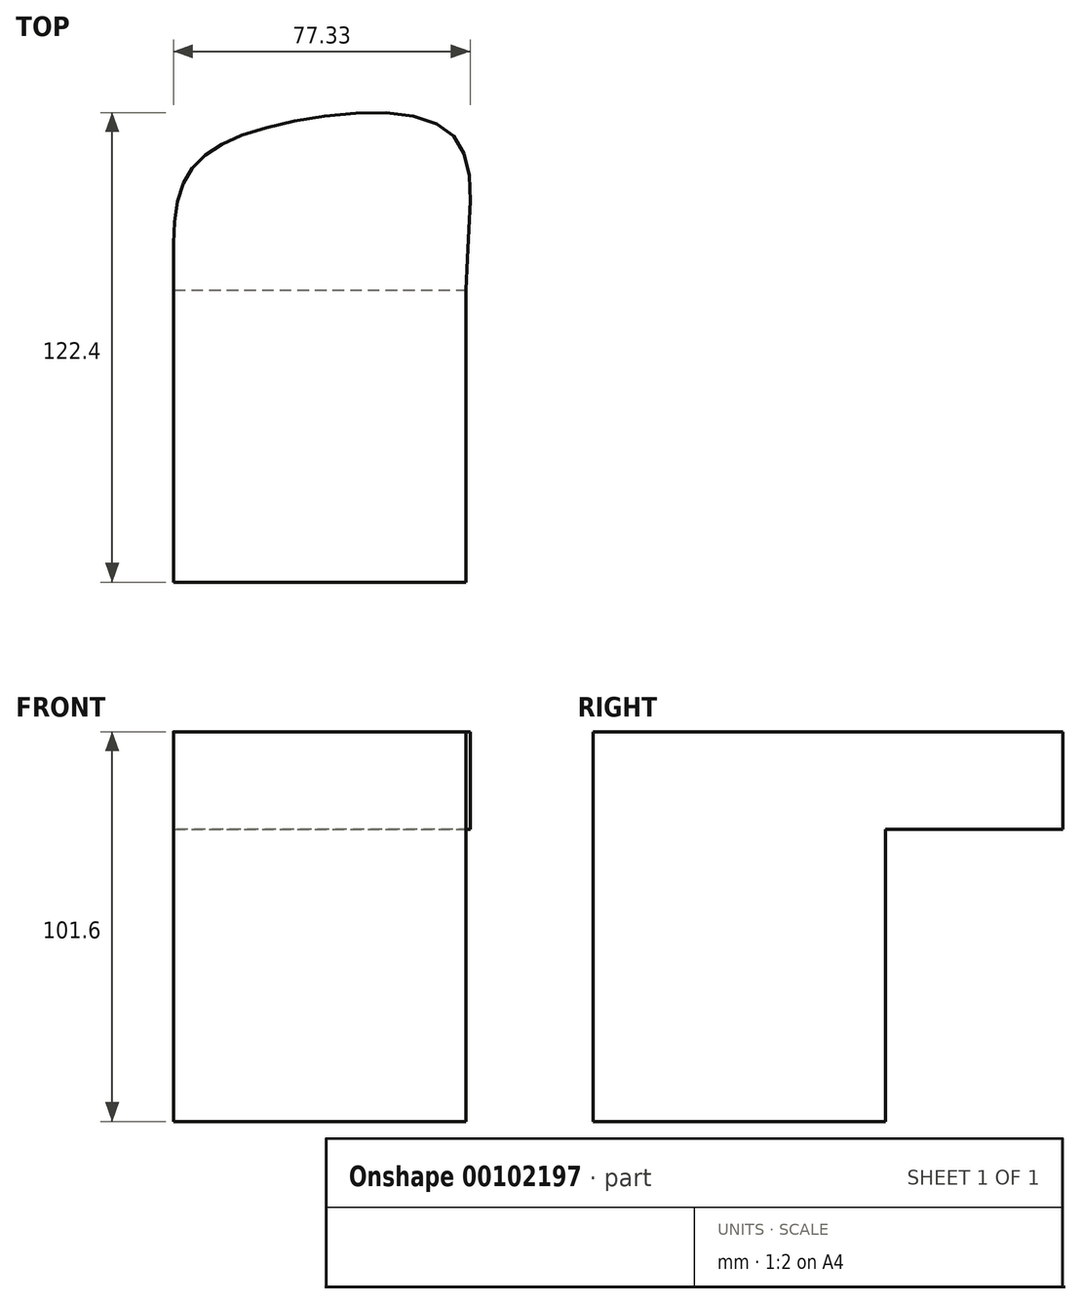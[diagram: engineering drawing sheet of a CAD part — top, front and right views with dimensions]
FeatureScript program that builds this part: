
annotation { "Feature Type Name" : "Feature", "Feature Type Description" : "" }
export const myFeature = defineFeature(function(context is Context, id is Id, definition is map)
    precondition{}
    {
        {
            var Q0;
            Q0=qCreatedBy(makeId("Front.planeOp"),FACE);
            var sketch = newSketch(context, id + "F0", { "sketchPlane" : qUnion([Q0])});
            skLineSegment(sketch, "E0.bottom", {"start": v(-38.1, 50.8) * mm, "end": v(38.1, 50.8) * mm});
            skLineSegment(sketch, "E0.top", {"start": v(-38.1, -50.8) * mm, "end": v(38.1, -50.8) * mm});
            skLineSegment(sketch, "E0.left", {"start": v(-38.1, 50.8) * mm, "end": v(-38.1, -50.8) * mm});
            skLineSegment(sketch, "E0.right", {"start": v(38.1, 50.8) * mm, "end": v(38.1, -50.8) * mm});
            skPoint(sketch, "E0.middle", {"position": v(0, 0) * mm});
            skSolve(sketch);
        }
        {
            var Q0;
            Q0 = qSketchRegion(id + "F0", true);
            extrude(context, id + "F1", {"entities" : qUnion([Q0]), "endBound" : BoundingType.SYMMETRIC, "depth" : 76.2 * mm});
        }
        {
            var Q0;
            Q0=makeQuery(id+"F1.opExtrude","SWEPT_FACE",FACE,{"disambiguationData":[OSD([sQuery(id+"F0.wireOp",EDGE,"E0.bottom")])]});
            var sketch = newSketch(context, id + "F2", { "sketchPlane" : qUnion([Q0])});
            skFitSpline(sketch, "E1", {"points": [v(38.1, 38.1) * mm, v(34.12, 78.87) * mm, v(-12.87, 80.67) * mm, v(-35.32, 66.6) * mm, v(-38.1, 38.1) * mm], "startDerivative": vector(0, 186.85) * mm, "endDerivative": vector(0, -141.2) * mm});
            skLineSegment(sketch, "E2", {"start": v(-38.1, 38.1) * mm, "end": v(38.1, 38.1) * mm});
            skSolve(sketch);
        }
        {
            var Q0;
            Q0 = qSketchRegion(id + "F2", true);
            extrude(context, id + "F3", {"entities" : qUnion([Q0]), "operationType" : NewBodyOperationType.ADD, "oppositeDirection" : true, "depth" : 25.4 * mm});
        }
    });
